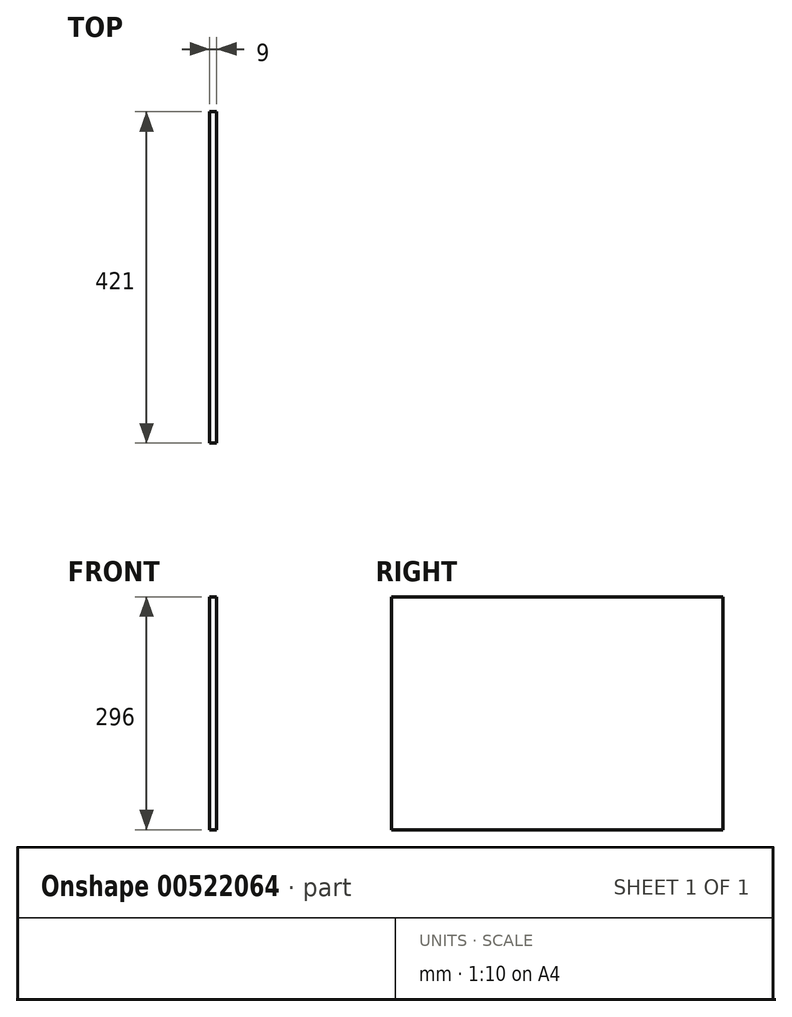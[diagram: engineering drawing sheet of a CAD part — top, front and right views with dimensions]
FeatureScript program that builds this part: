
annotation { "Feature Type Name" : "Feature", "Feature Type Description" : "" }
export const myFeature = defineFeature(function(context is Context, id is Id, definition is map)
    precondition{}
    {
        {
            var Q0;
            Q0=qCreatedBy(makeId("Right.planeOp"),FACE);
            var sketch = newSketch(context, id + "F0", { "sketchPlane" : qUnion([Q0])});
            skLineSegment(sketch, "E0.bottom", {"start": v(0, 0) * mm, "end": v(421, 0) * mm});
            skLineSegment(sketch, "E0.top", {"start": v(0, 296) * mm, "end": v(421, 296) * mm});
            skLineSegment(sketch, "E0.left", {"start": v(0, 0) * mm, "end": v(0, 296) * mm});
            skLineSegment(sketch, "E0.right", {"start": v(421, 0) * mm, "end": v(421, 296) * mm});
            skSolve(sketch);
        }
        {
            var Q0;
            Q0=makeQuery(id+"F0.imprint","IMPRINT",FACE,{"disambiguationData":[TD([[makeQuery(id+"F0.imprint","IMPRINT",EDGE,{"derivedFrom":sQuery(id+"F0.wireOp",EDGE,"E0.bottom")}),1.0]])]});
            extrude(context, id + "F1", {"entities" : qUnion([Q0]), "oppositeDirection" : true, "depth" : 9 * mm, "offsetDistance" : 25 * mm});
        }
    });
